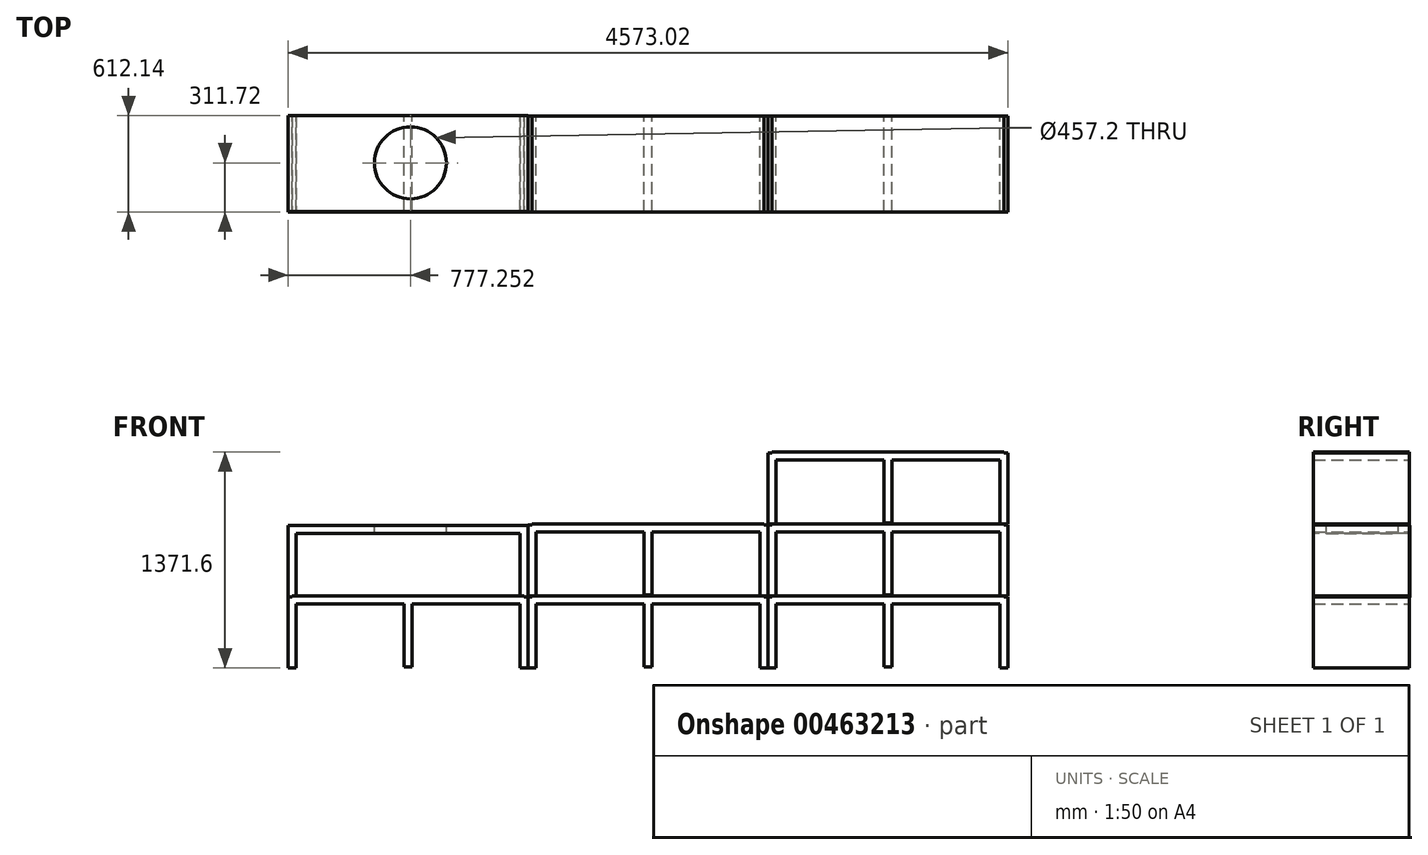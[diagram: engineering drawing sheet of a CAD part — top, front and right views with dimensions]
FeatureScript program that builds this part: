
annotation { "Feature Type Name" : "Feature", "Feature Type Description" : "" }
export const myFeature = defineFeature(function(context is Context, id is Id, definition is map)
    precondition{}
    {
        {
            var Q0;
            Q0=qCreatedBy(makeId("Front.planeOp"),FACE);
            var sketch = newSketch(context, id + "F0", { "sketchPlane" : qUnion([Q0])});
            skLineSegment(sketch, "E0", {"start": v(-1974.7, -123.48) * mm, "end": v(-1974.7, 327.37) * mm});
            skLineSegment(sketch, "E1", {"start": v(-1974.7, 327.37) * mm, "end": v(-1949.3, 327.37) * mm});
            skLineSegment(sketch, "E2", {"start": v(-1949.3, 327.37) * mm, "end": v(-1949.3, 333.72) * mm});
            skLineSegment(sketch, "E3", {"start": v(-1949.3, 333.72) * mm, "end": v(-476.1, 333.72) * mm});
            skLineSegment(sketch, "E4", {"start": v(-476.1, 333.72) * mm, "end": v(-476.1, 327.37) * mm});
            skLineSegment(sketch, "E5", {"start": v(-476.1, 327.37) * mm, "end": v(-450.7, 327.37) * mm});
            skLineSegment(sketch, "E6", {"start": v(-450.7, 327.37) * mm, "end": v(-450.7, -123.48) * mm});
            skLineSegment(sketch, "E7", {"start": v(-450.7, -123.48) * mm, "end": v(-501.5, -123.48) * mm});
            skLineSegment(sketch, "E8", {"start": v(-501.5, -123.48) * mm, "end": v(-501.5, 282.92) * mm});
            skLineSegment(sketch, "E9", {"start": v(-501.5, 282.92) * mm, "end": v(-1187.3, 282.92) * mm});
            skLineSegment(sketch, "E10", {"start": v(-1187.3, 282.92) * mm, "end": v(-1187.3, -117.13) * mm});
            skLineSegment(sketch, "E11", {"start": v(-1187.3, -117.13) * mm, "end": v(-1238.1, -117.13) * mm});
            skLineSegment(sketch, "E12", {"start": v(-1238.1, -117.13) * mm, "end": v(-1238.1, 282.92) * mm});
            skLineSegment(sketch, "E13", {"start": v(-1238.1, 282.92) * mm, "end": v(-1923.9, 282.92) * mm});
            skLineSegment(sketch, "E14", {"start": v(-1923.9, 282.92) * mm, "end": v(-1923.9, -123.48) * mm});
            skLineSegment(sketch, "E15", {"start": v(-1923.9, -123.48) * mm, "end": v(-1974.7, -123.48) * mm});
            skSolve(sketch);
        }
        {
            var Q0;
            Q0 = qSketchRegion(id + "F0", true);
            extrude(context, id + "F1", {"entities" : qUnion([Q0]), "depth" : 609.6 * mm});
        }
        {
            var Q0;
            Q0=makeQuery(id+"F1.opExtrude","CAP_FACE",FACE,{"disambiguationData":[OSD([sQuery(id+"F0.wireOp",EDGE,"E0"),sQuery(id+"F0.wireOp",EDGE,"E1"),sQuery(id+"F0.wireOp",EDGE,"E2"),sQuery(id+"F0.wireOp",EDGE,"E3"),sQuery(id+"F0.wireOp",EDGE,"E4"),sQuery(id+"F0.wireOp",EDGE,"E5"),sQuery(id+"F0.wireOp",EDGE,"E6"),sQuery(id+"F0.wireOp",EDGE,"E7"),sQuery(id+"F0.wireOp",EDGE,"E8"),sQuery(id+"F0.wireOp",EDGE,"E9"),sQuery(id+"F0.wireOp",EDGE,"E10"),sQuery(id+"F0.wireOp",EDGE,"E11"),sQuery(id+"F0.wireOp",EDGE,"E12"),sQuery(id+"F0.wireOp",EDGE,"E13"),sQuery(id+"F0.wireOp",EDGE,"E14"),sQuery(id+"F0.wireOp",EDGE,"E15")])],"isStart":false});
            var sketch = newSketch(context, id + "F2", { "sketchPlane" : qUnion([Q0])});
            skLineSegment(sketch, "E16", {"start": v(-1985.88, 531.58) * mm, "end": v(-1985.88, 988.78) * mm});
            skLineSegment(sketch, "E17", {"start": v(-1985.88, 988.78) * mm, "end": v(-461.88, 988.78) * mm});
            skLineSegment(sketch, "E18", {"start": v(-461.88, 988.78) * mm, "end": v(-461.88, 531.58) * mm});
            skLineSegment(sketch, "E19", {"start": v(-461.88, 531.58) * mm, "end": v(-487.28, 531.58) * mm});
            skLineSegment(sketch, "E20", {"start": v(-487.28, 531.58) * mm, "end": v(-487.28, 537.93) * mm});
            skLineSegment(sketch, "E21", {"start": v(-487.28, 537.93) * mm, "end": v(-512.68, 537.93) * mm});
            skLineSegment(sketch, "E22", {"start": v(-512.68, 537.93) * mm, "end": v(-512.68, 937.98) * mm});
            skLineSegment(sketch, "E23", {"start": v(-512.68, 937.98) * mm, "end": v(-1935.08, 937.98) * mm});
            skLineSegment(sketch, "E24", {"start": v(-1935.08, 937.98) * mm, "end": v(-1935.08, 537.93) * mm});
            skLineSegment(sketch, "E25", {"start": v(-1935.08, 537.93) * mm, "end": v(-1960.48, 537.93) * mm});
            skLineSegment(sketch, "E26", {"start": v(-1960.48, 537.93) * mm, "end": v(-1960.48, 531.58) * mm});
            skLineSegment(sketch, "E27", {"start": v(-1960.48, 531.58) * mm, "end": v(-1985.88, 531.58) * mm});
            skSolve(sketch);
        }
        {
            var Q0;
            Q0=makeQuery(id+"F2.imprint","IMPRINT",FACE,{"disambiguationData":[TD([[makeQuery(id+"F2.imprint","IMPRINT",EDGE,{"derivedFrom":sQuery(id+"F2.wireOp",EDGE,"E16")}),-1.0]])]});
            extrude(context, id + "F3", {"entities" : qUnion([Q0]), "depth" : -609.6 * mm});
        }
        {
            var Q0;
            Q0=makeQuery(id+"F3.opExtrude","SWEPT_FACE",FACE,{"disambiguationData":[OSD([sQuery(id+"F2.wireOp",EDGE,"E17")])]});
            var sketch = newSketch(context, id + "F4", { "sketchPlane" : qUnion([Q0])});
            skPoint(sketch, "E28", {"position": v(-1208.63, -300.42) * mm});
            skSolve(sketch);
        }
        {
            var Q0;
            Q0=sQuery(id+"F4.wireOp",VERTEX,"E28");
            var Q1;
            Q1=makeQuery(id+"F3.opExtrude","SWEPT_BODY",BODY,{"disambiguationData":[OSD([sQuery(id+"F2.wireOp",EDGE,"E16"),sQuery(id+"F2.wireOp",EDGE,"E17"),sQuery(id+"F2.wireOp",EDGE,"E18"),sQuery(id+"F2.wireOp",EDGE,"E19"),sQuery(id+"F2.wireOp",EDGE,"E20"),sQuery(id+"F2.wireOp",EDGE,"E21"),sQuery(id+"F2.wireOp",EDGE,"E22"),sQuery(id+"F2.wireOp",EDGE,"E23"),sQuery(id+"F2.wireOp",EDGE,"E24"),sQuery(id+"F2.wireOp",EDGE,"E25"),sQuery(id+"F2.wireOp",EDGE,"E26"),sQuery(id+"F2.wireOp",EDGE,"E27")])]});
            hole(context, id + "F5", {"style" : HoleStyle.SIMPLE, "endStyle" : HoleEndStyle.BLIND, "holeDiameter" : 457.2 * mm, "holeDepth" : 50.8 * mm, "isTappedThrough" : true, "tappedDepth" : 12.7 * mm, "tapClearance" : 3, "locations" : qUnion([Q0]), "scope" : qUnion([Q1])});
        }
        {
            var Q0;
            Q0=makeQuery(id+"F1.opExtrude","SWEPT_BODY",BODY,{"disambiguationData":[OSD([sQuery(id+"F0.wireOp",EDGE,"E0"),sQuery(id+"F0.wireOp",EDGE,"E1"),sQuery(id+"F0.wireOp",EDGE,"E2"),sQuery(id+"F0.wireOp",EDGE,"E3"),sQuery(id+"F0.wireOp",EDGE,"E4"),sQuery(id+"F0.wireOp",EDGE,"E5"),sQuery(id+"F0.wireOp",EDGE,"E6"),sQuery(id+"F0.wireOp",EDGE,"E7"),sQuery(id+"F0.wireOp",EDGE,"E8"),sQuery(id+"F0.wireOp",EDGE,"E9"),sQuery(id+"F0.wireOp",EDGE,"E10"),sQuery(id+"F0.wireOp",EDGE,"E11"),sQuery(id+"F0.wireOp",EDGE,"E12"),sQuery(id+"F0.wireOp",EDGE,"E13"),sQuery(id+"F0.wireOp",EDGE,"E14"),sQuery(id+"F0.wireOp",EDGE,"E15")])]});
            transform(context, id + "F6", {"entities" : qUnion([Q0]), "transformType" : TransformType.COPY});
        }
        {
            var Q0;
            Q0=makeQuery(id+"F6.opPattern","COPY",BODY,{"derivedFrom":makeQuery(id+"F1.opExtrude","SWEPT_BODY",BODY,{"disambiguationData":[OSD([sQuery(id+"F0.wireOp",EDGE,"E0"),sQuery(id+"F0.wireOp",EDGE,"E1"),sQuery(id+"F0.wireOp",EDGE,"E2"),sQuery(id+"F0.wireOp",EDGE,"E3"),sQuery(id+"F0.wireOp",EDGE,"E4"),sQuery(id+"F0.wireOp",EDGE,"E5"),sQuery(id+"F0.wireOp",EDGE,"E6"),sQuery(id+"F0.wireOp",EDGE,"E7"),sQuery(id+"F0.wireOp",EDGE,"E8"),sQuery(id+"F0.wireOp",EDGE,"E9"),sQuery(id+"F0.wireOp",EDGE,"E10"),sQuery(id+"F0.wireOp",EDGE,"E11"),sQuery(id+"F0.wireOp",EDGE,"E12"),sQuery(id+"F0.wireOp",EDGE,"E13"),sQuery(id+"F0.wireOp",EDGE,"E14"),sQuery(id+"F0.wireOp",EDGE,"E15")])]}),"instanceName":"1"});
            deleteBodies(context, id + "F7", {"entities" : qUnion([Q0])});
        }
        {
            var Q0;
            Q0=makeQuery(id+"F1.opExtrude","SWEPT_BODY",BODY,{"disambiguationData":[OSD([sQuery(id+"F0.wireOp",EDGE,"E0"),sQuery(id+"F0.wireOp",EDGE,"E1"),sQuery(id+"F0.wireOp",EDGE,"E2"),sQuery(id+"F0.wireOp",EDGE,"E3"),sQuery(id+"F0.wireOp",EDGE,"E4"),sQuery(id+"F0.wireOp",EDGE,"E5"),sQuery(id+"F0.wireOp",EDGE,"E6"),sQuery(id+"F0.wireOp",EDGE,"E7"),sQuery(id+"F0.wireOp",EDGE,"E8"),sQuery(id+"F0.wireOp",EDGE,"E9"),sQuery(id+"F0.wireOp",EDGE,"E10"),sQuery(id+"F0.wireOp",EDGE,"E11"),sQuery(id+"F0.wireOp",EDGE,"E12"),sQuery(id+"F0.wireOp",EDGE,"E13"),sQuery(id+"F0.wireOp",EDGE,"E14"),sQuery(id+"F0.wireOp",EDGE,"E15")])]});
            transform(context, id + "F8", {"entities" : qUnion([Q0]), "transformType" : TransformType.TRANSLATION_3D, "dx" : 1717.04 * mm, "dy" : 695.96 * mm, "dz" : 78.74 * mm, "makeCopy" : true});
        }
        {
            var Q0;
            Q0=makeQuery(id+"F3.opExtrude","SWEPT_BODY",BODY,{"disambiguationData":[OSD([sQuery(id+"F2.wireOp",EDGE,"E16"),sQuery(id+"F2.wireOp",EDGE,"E17"),sQuery(id+"F2.wireOp",EDGE,"E18"),sQuery(id+"F2.wireOp",EDGE,"E19"),sQuery(id+"F2.wireOp",EDGE,"E20"),sQuery(id+"F2.wireOp",EDGE,"E21"),sQuery(id+"F2.wireOp",EDGE,"E22"),sQuery(id+"F2.wireOp",EDGE,"E23"),sQuery(id+"F2.wireOp",EDGE,"E24"),sQuery(id+"F2.wireOp",EDGE,"E25"),sQuery(id+"F2.wireOp",EDGE,"E26"),sQuery(id+"F2.wireOp",EDGE,"E27")])]});
            transform(context, id + "F9", {"entities" : qUnion([Q0]), "transformType" : TransformType.TRANSLATION_3D, "dx" : 1727.2 * mm, "dy" : 698.5 * mm, "dz" : -127 * mm, "makeCopy" : true});
        }
        {
            var Q0;
            Q0=makeQuery(id+"F8.opPattern","COPY",BODY,{"derivedFrom":makeQuery(id+"F1.opExtrude","SWEPT_BODY",BODY,{"disambiguationData":[OSD([sQuery(id+"F0.wireOp",EDGE,"E0"),sQuery(id+"F0.wireOp",EDGE,"E1"),sQuery(id+"F0.wireOp",EDGE,"E2"),sQuery(id+"F0.wireOp",EDGE,"E3"),sQuery(id+"F0.wireOp",EDGE,"E4"),sQuery(id+"F0.wireOp",EDGE,"E5"),sQuery(id+"F0.wireOp",EDGE,"E6"),sQuery(id+"F0.wireOp",EDGE,"E7"),sQuery(id+"F0.wireOp",EDGE,"E8"),sQuery(id+"F0.wireOp",EDGE,"E9"),sQuery(id+"F0.wireOp",EDGE,"E10"),sQuery(id+"F0.wireOp",EDGE,"E11"),sQuery(id+"F0.wireOp",EDGE,"E12"),sQuery(id+"F0.wireOp",EDGE,"E13"),sQuery(id+"F0.wireOp",EDGE,"E14"),sQuery(id+"F0.wireOp",EDGE,"E15")])]}),"instanceName":"1"});
            transform(context, id + "F10", {"entities" : qUnion([Q0]), "transformType" : TransformType.TRANSLATION_3D, "dx" : 1524 * mm, "dy" : 0 * mm, "dz" : 0 * mm, "makeCopy" : true});
        }
        {
            var Q0;
            Q0=makeQuery(id+"F10.opPattern","COPY",BODY,{"derivedFrom":makeQuery(id+"F8.opPattern","COPY",BODY,{"derivedFrom":makeQuery(id+"F1.opExtrude","SWEPT_BODY",BODY,{"disambiguationData":[OSD([sQuery(id+"F0.wireOp",EDGE,"E0"),sQuery(id+"F0.wireOp",EDGE,"E1"),sQuery(id+"F0.wireOp",EDGE,"E2"),sQuery(id+"F0.wireOp",EDGE,"E3"),sQuery(id+"F0.wireOp",EDGE,"E4"),sQuery(id+"F0.wireOp",EDGE,"E5"),sQuery(id+"F0.wireOp",EDGE,"E6"),sQuery(id+"F0.wireOp",EDGE,"E7"),sQuery(id+"F0.wireOp",EDGE,"E8"),sQuery(id+"F0.wireOp",EDGE,"E9"),sQuery(id+"F0.wireOp",EDGE,"E10"),sQuery(id+"F0.wireOp",EDGE,"E11"),sQuery(id+"F0.wireOp",EDGE,"E12"),sQuery(id+"F0.wireOp",EDGE,"E13"),sQuery(id+"F0.wireOp",EDGE,"E14"),sQuery(id+"F0.wireOp",EDGE,"E15")])]}),"instanceName":"1"}),"instanceName":"1"});
            transform(context, id + "F11", {"entities" : qUnion([Q0]), "transformType" : TransformType.TRANSLATION_3D, "dx" : 0 * mm, "dy" : 0 * mm, "dz" : 457.2 * mm, "makeCopy" : true});
        }
        {
            var Q0;
            Q0=makeQuery(id+"F10.opPattern","COPY",BODY,{"derivedFrom":makeQuery(id+"F8.opPattern","COPY",BODY,{"derivedFrom":makeQuery(id+"F1.opExtrude","SWEPT_BODY",BODY,{"disambiguationData":[OSD([sQuery(id+"F0.wireOp",EDGE,"E0"),sQuery(id+"F0.wireOp",EDGE,"E1"),sQuery(id+"F0.wireOp",EDGE,"E2"),sQuery(id+"F0.wireOp",EDGE,"E3"),sQuery(id+"F0.wireOp",EDGE,"E4"),sQuery(id+"F0.wireOp",EDGE,"E5"),sQuery(id+"F0.wireOp",EDGE,"E6"),sQuery(id+"F0.wireOp",EDGE,"E7"),sQuery(id+"F0.wireOp",EDGE,"E8"),sQuery(id+"F0.wireOp",EDGE,"E9"),sQuery(id+"F0.wireOp",EDGE,"E10"),sQuery(id+"F0.wireOp",EDGE,"E11"),sQuery(id+"F0.wireOp",EDGE,"E12"),sQuery(id+"F0.wireOp",EDGE,"E13"),sQuery(id+"F0.wireOp",EDGE,"E14"),sQuery(id+"F0.wireOp",EDGE,"E15")])]}),"instanceName":"1"}),"instanceName":"1"});
            var Q1;
            Q1=makeQuery(id+"F11.opPattern","COPY",BODY,{"derivedFrom":makeQuery(id+"F10.opPattern","COPY",BODY,{"derivedFrom":makeQuery(id+"F8.opPattern","COPY",BODY,{"derivedFrom":makeQuery(id+"F1.opExtrude","SWEPT_BODY",BODY,{"disambiguationData":[OSD([sQuery(id+"F0.wireOp",EDGE,"E0"),sQuery(id+"F0.wireOp",EDGE,"E1"),sQuery(id+"F0.wireOp",EDGE,"E2"),sQuery(id+"F0.wireOp",EDGE,"E3"),sQuery(id+"F0.wireOp",EDGE,"E4"),sQuery(id+"F0.wireOp",EDGE,"E5"),sQuery(id+"F0.wireOp",EDGE,"E6"),sQuery(id+"F0.wireOp",EDGE,"E7"),sQuery(id+"F0.wireOp",EDGE,"E8"),sQuery(id+"F0.wireOp",EDGE,"E9"),sQuery(id+"F0.wireOp",EDGE,"E10"),sQuery(id+"F0.wireOp",EDGE,"E11"),sQuery(id+"F0.wireOp",EDGE,"E12"),sQuery(id+"F0.wireOp",EDGE,"E13"),sQuery(id+"F0.wireOp",EDGE,"E14"),sQuery(id+"F0.wireOp",EDGE,"E15")])]}),"instanceName":"1"}),"instanceName":"1"}),"instanceName":"1"});
            transform(context, id + "F12", {"entities" : qUnion([Q0, Q1]), "transformType" : TransformType.TRANSLATION_3D, "dx" : 1524 * mm, "dy" : 0 * mm, "dz" : 0 * mm, "makeCopy" : true});
        }
        {
            var Q0;
            Q0=makeQuery(id+"F12.opPattern","COPY",BODY,{"derivedFrom":makeQuery(id+"F11.opPattern","COPY",BODY,{"derivedFrom":makeQuery(id+"F10.opPattern","COPY",BODY,{"derivedFrom":makeQuery(id+"F8.opPattern","COPY",BODY,{"derivedFrom":makeQuery(id+"F1.opExtrude","SWEPT_BODY",BODY,{"disambiguationData":[OSD([sQuery(id+"F0.wireOp",EDGE,"E0"),sQuery(id+"F0.wireOp",EDGE,"E1"),sQuery(id+"F0.wireOp",EDGE,"E2"),sQuery(id+"F0.wireOp",EDGE,"E3"),sQuery(id+"F0.wireOp",EDGE,"E4"),sQuery(id+"F0.wireOp",EDGE,"E5"),sQuery(id+"F0.wireOp",EDGE,"E6"),sQuery(id+"F0.wireOp",EDGE,"E7"),sQuery(id+"F0.wireOp",EDGE,"E8"),sQuery(id+"F0.wireOp",EDGE,"E9"),sQuery(id+"F0.wireOp",EDGE,"E10"),sQuery(id+"F0.wireOp",EDGE,"E11"),sQuery(id+"F0.wireOp",EDGE,"E12"),sQuery(id+"F0.wireOp",EDGE,"E13"),sQuery(id+"F0.wireOp",EDGE,"E14"),sQuery(id+"F0.wireOp",EDGE,"E15")])]}),"instanceName":"1"}),"instanceName":"1"}),"instanceName":"1"}),"instanceName":"1"});
            transform(context, id + "F13", {"entities" : qUnion([Q0]), "transformType" : TransformType.TRANSLATION_3D, "dx" : 0 * mm, "dy" : 0 * mm, "dz" : 457.2 * mm, "makeCopy" : true});
        }
        {
            var Q0;
            Q0=makeQuery(id+"F11.opPattern","COPY",BODY,{"derivedFrom":makeQuery(id+"F10.opPattern","COPY",BODY,{"derivedFrom":makeQuery(id+"F8.opPattern","COPY",BODY,{"derivedFrom":makeQuery(id+"F1.opExtrude","SWEPT_BODY",BODY,{"disambiguationData":[OSD([sQuery(id+"F0.wireOp",EDGE,"E0"),sQuery(id+"F0.wireOp",EDGE,"E1"),sQuery(id+"F0.wireOp",EDGE,"E2"),sQuery(id+"F0.wireOp",EDGE,"E3"),sQuery(id+"F0.wireOp",EDGE,"E4"),sQuery(id+"F0.wireOp",EDGE,"E5"),sQuery(id+"F0.wireOp",EDGE,"E6"),sQuery(id+"F0.wireOp",EDGE,"E7"),sQuery(id+"F0.wireOp",EDGE,"E8"),sQuery(id+"F0.wireOp",EDGE,"E9"),sQuery(id+"F0.wireOp",EDGE,"E10"),sQuery(id+"F0.wireOp",EDGE,"E11"),sQuery(id+"F0.wireOp",EDGE,"E12"),sQuery(id+"F0.wireOp",EDGE,"E13"),sQuery(id+"F0.wireOp",EDGE,"E14"),sQuery(id+"F0.wireOp",EDGE,"E15")])]}),"instanceName":"1"}),"instanceName":"1"}),"instanceName":"1"});
            deleteBodies(context, id + "F14", {"entities" : qUnion([Q0])});
        }
        {
            var Q0;
            Q0=makeQuery(id+"F12.opPattern","COPY",BODY,{"derivedFrom":makeQuery(id+"F11.opPattern","COPY",BODY,{"derivedFrom":makeQuery(id+"F10.opPattern","COPY",BODY,{"derivedFrom":makeQuery(id+"F8.opPattern","COPY",BODY,{"derivedFrom":makeQuery(id+"F1.opExtrude","SWEPT_BODY",BODY,{"disambiguationData":[OSD([sQuery(id+"F0.wireOp",EDGE,"E0"),sQuery(id+"F0.wireOp",EDGE,"E1"),sQuery(id+"F0.wireOp",EDGE,"E2"),sQuery(id+"F0.wireOp",EDGE,"E3"),sQuery(id+"F0.wireOp",EDGE,"E4"),sQuery(id+"F0.wireOp",EDGE,"E5"),sQuery(id+"F0.wireOp",EDGE,"E6"),sQuery(id+"F0.wireOp",EDGE,"E7"),sQuery(id+"F0.wireOp",EDGE,"E8"),sQuery(id+"F0.wireOp",EDGE,"E9"),sQuery(id+"F0.wireOp",EDGE,"E10"),sQuery(id+"F0.wireOp",EDGE,"E11"),sQuery(id+"F0.wireOp",EDGE,"E12"),sQuery(id+"F0.wireOp",EDGE,"E13"),sQuery(id+"F0.wireOp",EDGE,"E14"),sQuery(id+"F0.wireOp",EDGE,"E15")])]}),"instanceName":"1"}),"instanceName":"1"}),"instanceName":"1"}),"instanceName":"1"});
            transform(context, id + "F15", {"entities" : qUnion([Q0]), "transformType" : TransformType.TRANSLATION_3D, "dx" : -1524 * mm, "dy" : 0 * mm, "dz" : 0 * mm, "makeCopy" : true});
        }
        {
            var Q0;
            Q0=makeQuery(id+"F13.opPattern","COPY",FACE,{"derivedFrom":makeQuery(id+"F12.opPattern","COPY",FACE,{"derivedFrom":makeQuery(id+"F11.opPattern","COPY",FACE,{"derivedFrom":makeQuery(id+"F10.opPattern","COPY",FACE,{"derivedFrom":makeQuery(id+"F8.opPattern","COPY",FACE,{"derivedFrom":makeQuery(id+"F1.opExtrude","CAP_FACE",FACE,{"disambiguationData":[OSD([sQuery(id+"F0.wireOp",EDGE,"E0"),sQuery(id+"F0.wireOp",EDGE,"E1"),sQuery(id+"F0.wireOp",EDGE,"E2"),sQuery(id+"F0.wireOp",EDGE,"E3"),sQuery(id+"F0.wireOp",EDGE,"E4"),sQuery(id+"F0.wireOp",EDGE,"E5"),sQuery(id+"F0.wireOp",EDGE,"E6"),sQuery(id+"F0.wireOp",EDGE,"E7"),sQuery(id+"F0.wireOp",EDGE,"E8"),sQuery(id+"F0.wireOp",EDGE,"E9"),sQuery(id+"F0.wireOp",EDGE,"E10"),sQuery(id+"F0.wireOp",EDGE,"E11"),sQuery(id+"F0.wireOp",EDGE,"E12"),sQuery(id+"F0.wireOp",EDGE,"E13"),sQuery(id+"F0.wireOp",EDGE,"E14"),sQuery(id+"F0.wireOp",EDGE,"E15")])],"isStart":true}),"instanceName":"1"}),"instanceName":"1"}),"instanceName":"1"}),"instanceName":"1"}),"instanceName":"1"});
            var sketch = newSketch(context, id + "F16", { "sketchPlane" : qUnion([Q0])});
            skSolve(sketch);
        }
        {
            var Q0;
            Q0=makeQuery(id+"F16.imprint","IMPRINT",FACE,{"disambiguationData":[TD([[makeQuery(id+"F16.imprint","IMPRINT",EDGE,{"derivedFrom":makeQuery(id+"F13.opPattern","COPY",EDGE,{"derivedFrom":makeQuery(id+"F12.opPattern","COPY",EDGE,{"derivedFrom":makeQuery(id+"F11.opPattern","COPY",EDGE,{"derivedFrom":makeQuery(id+"F10.opPattern","COPY",EDGE,{"derivedFrom":makeQuery(id+"F8.opPattern","COPY",EDGE,{"derivedFrom":makeQuery(id+"F1.opExtrude","CAP_EDGE",EDGE,{"disambiguationData":[OSD([sQuery(id+"F0.wireOp",EDGE,"E0")])],"isStart":true}),"instanceName":"1"}),"instanceName":"1"}),"instanceName":"1"}),"instanceName":"1"}),"instanceName":"1"})}),1.0]])]});
            var sketch = newSketch(context, id + "F17", { "sketchPlane" : qUnion([Q0])});
            skLineSegment(sketch, "E29.bottom", {"start": v(-4321.29, 1333.46) * mm, "end": v(-2797.29, 1333.46) * mm});
            skLineSegment(sketch, "E29.top", {"start": v(-4321.29, -38.14) * mm, "end": v(-2797.29, -38.14) * mm});
            skLineSegment(sketch, "E29.left", {"start": v(-4321.29, 1333.46) * mm, "end": v(-4321.29, -38.14) * mm});
            skLineSegment(sketch, "E29.right", {"start": v(-2797.29, 1333.46) * mm, "end": v(-2797.29, -38.14) * mm});
            skSolve(sketch);
        }
        {
            var Q0;
            Q0 = qSketchRegion(id + "F17", true);
            extrude(context, id + "F18", {"entities" : qUnion([Q0]), "depth" : 6.35 * mm});
        }
        {
            var Q0;
            Q0=makeQuery(id+"F15.opPattern","COPY",FACE,{"derivedFrom":makeQuery(id+"F12.opPattern","COPY",FACE,{"derivedFrom":makeQuery(id+"F11.opPattern","COPY",FACE,{"derivedFrom":makeQuery(id+"F10.opPattern","COPY",FACE,{"derivedFrom":makeQuery(id+"F8.opPattern","COPY",FACE,{"derivedFrom":makeQuery(id+"F1.opExtrude","CAP_FACE",FACE,{"disambiguationData":[OSD([sQuery(id+"F0.wireOp",EDGE,"E0"),sQuery(id+"F0.wireOp",EDGE,"E1"),sQuery(id+"F0.wireOp",EDGE,"E2"),sQuery(id+"F0.wireOp",EDGE,"E3"),sQuery(id+"F0.wireOp",EDGE,"E4"),sQuery(id+"F0.wireOp",EDGE,"E5"),sQuery(id+"F0.wireOp",EDGE,"E6"),sQuery(id+"F0.wireOp",EDGE,"E7"),sQuery(id+"F0.wireOp",EDGE,"E8"),sQuery(id+"F0.wireOp",EDGE,"E9"),sQuery(id+"F0.wireOp",EDGE,"E10"),sQuery(id+"F0.wireOp",EDGE,"E11"),sQuery(id+"F0.wireOp",EDGE,"E12"),sQuery(id+"F0.wireOp",EDGE,"E13"),sQuery(id+"F0.wireOp",EDGE,"E14"),sQuery(id+"F0.wireOp",EDGE,"E15")])],"isStart":true}),"instanceName":"1"}),"instanceName":"1"}),"instanceName":"1"}),"instanceName":"1"}),"instanceName":"1"});
            var sketch = newSketch(context, id + "F19", { "sketchPlane" : qUnion([Q0])});
            skLineSegment(sketch, "E30.bottom", {"start": v(-2790.34, 863.31) * mm, "end": v(257.66, 863.31) * mm});
            skLineSegment(sketch, "E30.top", {"start": v(-2790.34, -51.09) * mm, "end": v(257.66, -51.09) * mm});
            skLineSegment(sketch, "E30.left", {"start": v(-2790.34, 863.31) * mm, "end": v(-2790.34, -51.09) * mm});
            skLineSegment(sketch, "E30.right", {"start": v(257.66, 863.31) * mm, "end": v(257.66, -51.09) * mm});
            skSolve(sketch);
        }
        {
            var Q0;
            Q0 = qSketchRegion(id + "F19", true);
            extrude(context, id + "F20", {"entities" : qUnion([Q0]), "depth" : 6.35 * mm});
        }
        {
            var Q0;
            Q0=makeQuery(id+"F20.opExtrude","SWEPT_BODY",BODY,{"disambiguationData":[OSD([sQuery(id+"F19.wireOp",EDGE,"E30.bottom"),sQuery(id+"F19.wireOp",EDGE,"E30.top"),sQuery(id+"F19.wireOp",EDGE,"E30.left"),sQuery(id+"F19.wireOp",EDGE,"E30.right")])]});
            deleteBodies(context, id + "F21", {"entities" : qUnion([Q0])});
        }
        {
            var Q0;
            Q0=makeQuery(id+"F18.opExtrude","SWEPT_BODY",BODY,{"disambiguationData":[OSD([sQuery(id+"F17.wireOp",EDGE,"E29.bottom"),sQuery(id+"F17.wireOp",EDGE,"E29.top"),sQuery(id+"F17.wireOp",EDGE,"E29.left"),sQuery(id+"F17.wireOp",EDGE,"E29.right")])]});
            deleteBodies(context, id + "F22", {"entities" : qUnion([Q0])});
        }
        {
            var Q0;
            Q0=makeQuery(id+"F1.opExtrude","SWEPT_BODY",BODY,{"disambiguationData":[OSD([sQuery(id+"F0.wireOp",EDGE,"E0"),sQuery(id+"F0.wireOp",EDGE,"E1"),sQuery(id+"F0.wireOp",EDGE,"E2"),sQuery(id+"F0.wireOp",EDGE,"E3"),sQuery(id+"F0.wireOp",EDGE,"E4"),sQuery(id+"F0.wireOp",EDGE,"E5"),sQuery(id+"F0.wireOp",EDGE,"E6"),sQuery(id+"F0.wireOp",EDGE,"E7"),sQuery(id+"F0.wireOp",EDGE,"E8"),sQuery(id+"F0.wireOp",EDGE,"E9"),sQuery(id+"F0.wireOp",EDGE,"E10"),sQuery(id+"F0.wireOp",EDGE,"E11"),sQuery(id+"F0.wireOp",EDGE,"E12"),sQuery(id+"F0.wireOp",EDGE,"E13"),sQuery(id+"F0.wireOp",EDGE,"E14"),sQuery(id+"F0.wireOp",EDGE,"E15")])]});
            deleteBodies(context, id + "F23", {"entities" : qUnion([Q0])});
        }
        {
            var Q0;
            Q0=makeQuery(id+"F3.opExtrude","SWEPT_BODY",BODY,{"disambiguationData":[OSD([sQuery(id+"F2.wireOp",EDGE,"E16"),sQuery(id+"F2.wireOp",EDGE,"E17"),sQuery(id+"F2.wireOp",EDGE,"E18"),sQuery(id+"F2.wireOp",EDGE,"E19"),sQuery(id+"F2.wireOp",EDGE,"E20"),sQuery(id+"F2.wireOp",EDGE,"E21"),sQuery(id+"F2.wireOp",EDGE,"E22"),sQuery(id+"F2.wireOp",EDGE,"E23"),sQuery(id+"F2.wireOp",EDGE,"E24"),sQuery(id+"F2.wireOp",EDGE,"E25"),sQuery(id+"F2.wireOp",EDGE,"E26"),sQuery(id+"F2.wireOp",EDGE,"E27")])]});
            deleteBodies(context, id + "F24", {"entities" : qUnion([Q0])});
        }
    });
